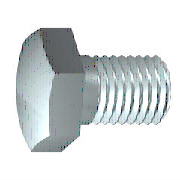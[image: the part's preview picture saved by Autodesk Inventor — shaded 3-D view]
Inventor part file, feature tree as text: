
AUTODESK INVENTOR PART (.ipt)
format: ipt  version: 2013 (Build 170138000, 138)  size: 188,416 bytes
history: native  units: mm (DEFAULTED — no unit token found)
features: sketch x2, extrude x1, chamfer x1, plane x1
ambient origin geometry x7: Origin, YZ Plane, XZ Plane, X Axis, Y Axis, Z Axis, Center Point
bodies: Solid1 (feature_tree), Body (feature_tree)
feature tree (5):
  extrude  "Head"  TaperAngle=90.0deg  [1 undecoded]
  chamfer  "Chamfer1"  [1 undecoded]
  plane  "Work Plane1"
  sketch  "Sketch1"  dims[d2=8.0mm d12=90.0deg]
  sketch  "Sketch2"  dims[d3=5.68mm d4=0.0mm d21=90.0deg d6=0.766813mm d7=0.766912mm d8=0.0mm d11=13.0mm d15=22.0mm d16=0.0mm d55=45.0deg d58=0.0mm d59=70.0mm d65=13.0mm d67=30.0deg d68=15.6mm d69=5.68mm d71=0.1mm d73=0.0mm]
note: 2 required parameter values undecoded (feature->parameter linkage not recoverable at this tier; creation-order binding heuristic only, values carry confidence <= 0.55)
